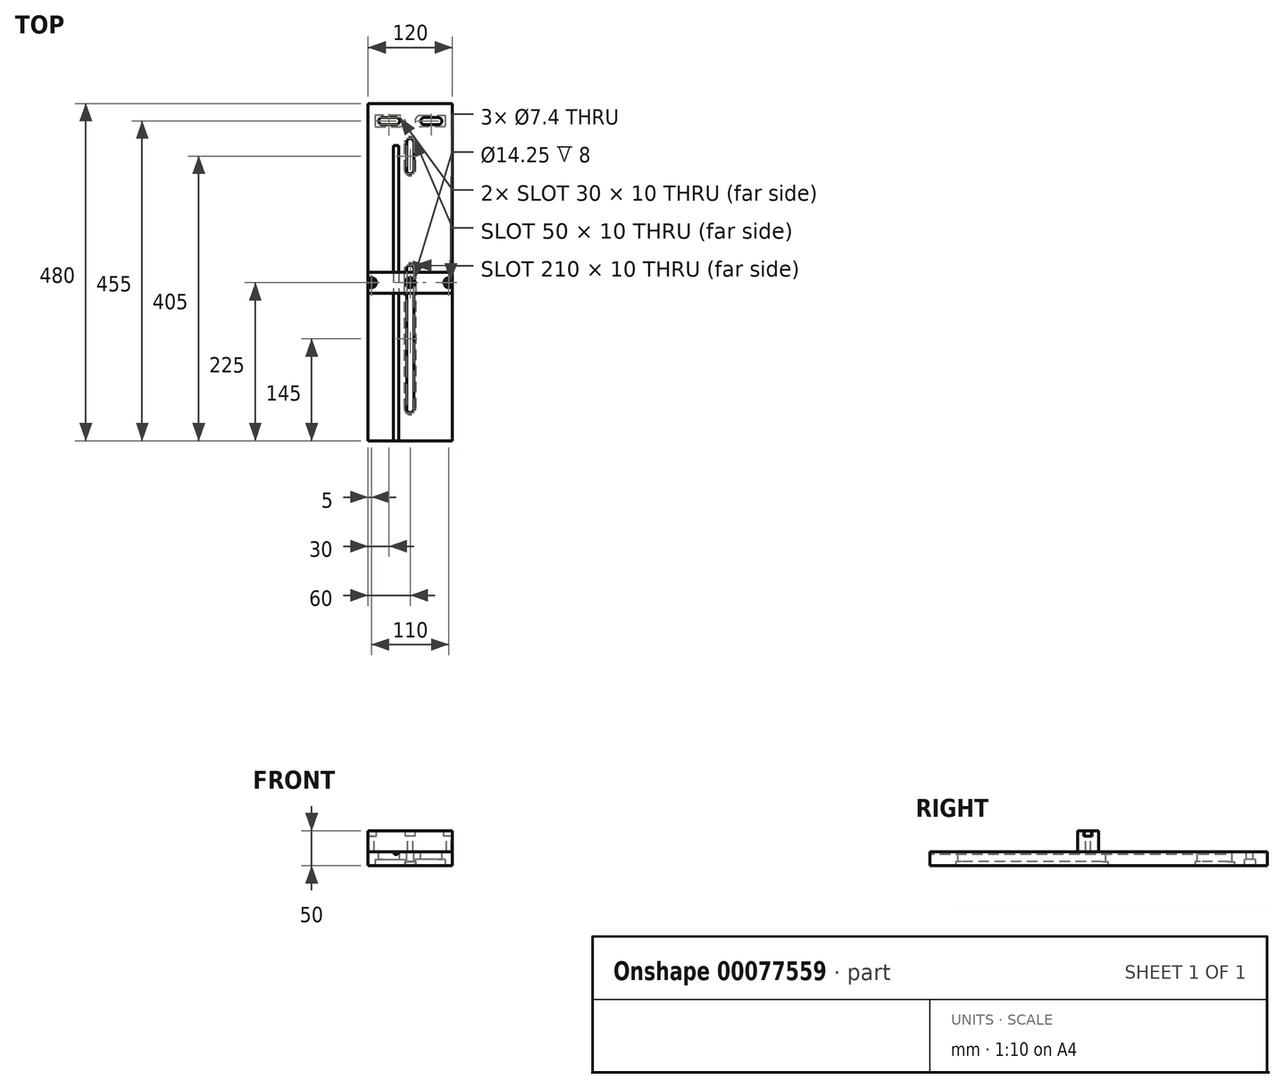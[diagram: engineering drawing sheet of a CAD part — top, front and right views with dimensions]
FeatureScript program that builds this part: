
annotation { "Feature Type Name" : "Feature", "Feature Type Description" : "" }
export const myFeature = defineFeature(function(context is Context, id is Id, definition is map)
    precondition{}
    {
        {
            var Q0;
            Q0=qCreatedBy(makeId("Front.planeOp"),FACE);
            var sketch = newSketch(context, id + "F0", { "sketchPlane" : qUnion([Q0])});
            skLineSegment(sketch, "E0.bottom", {"start": v(-60, 0) * mm, "end": v(60, 0) * mm});
            skLineSegment(sketch, "E0.top", {"start": v(-60, 20) * mm, "end": v(60, 20) * mm});
            skLineSegment(sketch, "E0.left", {"start": v(-60, 0) * mm, "end": v(-60, 20) * mm});
            skLineSegment(sketch, "E0.right", {"start": v(60, 0) * mm, "end": v(60, 20) * mm});
            skSolve(sketch);
        }
        {
            var Q0;
            Q0=makeQuery(id+"F0.imprint","IMPRINT",FACE,{"disambiguationData":[TD([[makeQuery(id+"F0.imprint","IMPRINT",EDGE,{"derivedFrom":sQuery(id+"F0.wireOp",EDGE,"E0.bottom")}),1.0]])]});
            extrude(context, id + "F1", {"entities" : qUnion([Q0]), "oppositeDirection" : true, "depth" : 480 * mm});
        }
        {
            var Q0;
            Q0=makeQuery(id+"F1.opExtrude","SWEPT_FACE",FACE,{"disambiguationData":[OSD([sQuery(id+"F0.wireOp",EDGE,"E0.top")])]});
            var sketch = newSketch(context, id + "F2", { "sketchPlane" : qUnion([Q0])});
            skLineSegment(sketch, "E1", {"start": v(-5, 245) * mm, "end": v(-5, 45) * mm});
            skArc(sketch, "E2", {"start": v(-5, 45) * mm, "mid": v(0, 40) * mm, "end": v(5, 45) * mm});
            skLineSegment(sketch, "E3", {"start": v(5, 45) * mm, "end": v(5, 245) * mm});
            skArc(sketch, "E4", {"start": v(5, 245) * mm, "mid": v(0, 250) * mm, "end": v(-5, 245) * mm});
            skLineSegment(sketch, "E5", {"start": v(0, 425) * mm, "end": v(0, 385) * mm});
            skArc(sketch, "E6.0.startCap", {"start": v(-5, 425) * mm, "mid": v(0, 430) * mm, "end": v(5, 425) * mm});
            skArc(sketch, "E6.0.endCap", {"start": v(5, 385) * mm, "mid": v(0, 380) * mm, "end": v(-5, 385) * mm});
            skLineSegment(sketch, "E6.0.left", {"start": v(5, 425) * mm, "end": v(5, 385) * mm});
            skLineSegment(sketch, "E6.0.right", {"start": v(-5, 425) * mm, "end": v(-5, 385) * mm});
            skSolve(sketch);
        }
        {
            var Q0;
            Q0 = qSketchRegion(id + "F2", true);
            extrude(context, id + "F3", {"entities" : qUnion([Q0]), "operationType" : NewBodyOperationType.REMOVE, "endBound" : BoundingType.THROUGH_ALL, "oppositeDirection" : true, "depth" : 25 * mm});
        }
        {
            var Q0;
            Q0=makeQuery(id+"F1.opExtrude","SWEPT_FACE",FACE,{"disambiguationData":[OSD([sQuery(id+"F0.wireOp",EDGE,"E0.bottom")])]});
            var sketch = newSketch(context, id + "F4", { "sketchPlane" : qUnion([Q0])});
            skArc(sketch, "E7.0", {"start": v(8, -45) * mm, "mid": v(0, -37) * mm, "end": v(-8, -45) * mm});
            skLineSegment(sketch, "E7.1", {"start": v(8, -245) * mm, "end": v(8, -45) * mm});
            skArc(sketch, "E7.2", {"start": v(-8, -245) * mm, "mid": v(0, -253) * mm, "end": v(8, -245) * mm});
            skLineSegment(sketch, "E7.3", {"start": v(-8, -45) * mm, "end": v(-8, -245) * mm});
            skLineSegment(sketch, "E8.0", {"start": v(-8, -385) * mm, "end": v(-8, -425) * mm});
            skArc(sketch, "E8.1", {"start": v(-8, -385) * mm, "mid": v(0, -377) * mm, "end": v(8, -385) * mm});
            skLineSegment(sketch, "E8.2", {"start": v(8, -385) * mm, "end": v(8, -425) * mm});
            skArc(sketch, "E8.3", {"start": v(8, -425) * mm, "mid": v(0, -433) * mm, "end": v(-8, -425) * mm});
            skSolve(sketch);
        }
        {
            var Q0;
            Q0 = qSketchRegion(id + "F4", true);
            extrude(context, id + "F5", {"entities" : qUnion([Q0]), "operationType" : NewBodyOperationType.REMOVE, "oppositeDirection" : true, "depth" : 6.1 * mm});
        }
        {
            var Q0;
            Q0=makeQuery(id+"F1.opExtrude","SWEPT_FACE",FACE,{"disambiguationData":[OSD([sQuery(id+"F0.wireOp",EDGE,"E0.top")])]});
            var sketch = newSketch(context, id + "F6", { "sketchPlane" : qUnion([Q0])});
            skLineSegment(sketch, "E9.bottom", {"start": v(-40, 450) * mm, "end": v(-20, 450) * mm});
            skLineSegment(sketch, "E9.top", {"start": v(-40, 460) * mm, "end": v(-20, 460) * mm});
            skLineSegment(sketch, "E9.left", {"start": v(-45, 455) * mm, "end": v(-45, 455) * mm});
            skLineSegment(sketch, "E9.right", {"start": v(-15, 455) * mm, "end": v(-15, 455) * mm});
            skPoint(sketch, "E10.visualSharp", {"position": v(-45, 460) * mm});
            skArc(sketch, "E10.filletArc", {"start": v(-40, 460) * mm, "mid": v(-43.54, 458.54) * mm, "end": v(-45, 455) * mm});
            skPoint(sketch, "E11.visualSharp", {"position": v(-45, 450) * mm});
            skArc(sketch, "E11.filletArc", {"start": v(-45, 455) * mm, "mid": v(-43.54, 451.46) * mm, "end": v(-40, 450) * mm});
            skPoint(sketch, "E12.visualSharp", {"position": v(-15, 450) * mm});
            skArc(sketch, "E12.filletArc", {"start": v(-20, 450) * mm, "mid": v(-16.46, 451.46) * mm, "end": v(-15, 455) * mm});
            skPoint(sketch, "E13.visualSharp", {"position": v(-15, 460) * mm});
            skArc(sketch, "E13.filletArc", {"start": v(-15, 455) * mm, "mid": v(-16.46, 458.54) * mm, "end": v(-20, 460) * mm});
            skLineSegment(sketch, "E14.MirrorCS", {"start": v(40, 460) * mm, "end": v(20, 460) * mm});
            skArc(sketch, "E15.MirrorCS", {"start": v(15, 455) * mm, "mid": v(16.46, 458.54) * mm, "end": v(20, 460) * mm});
            skArc(sketch, "E16.MirrorCS", {"start": v(20, 450) * mm, "mid": v(16.46, 451.46) * mm, "end": v(15, 455) * mm});
            skLineSegment(sketch, "E17.MirrorCS", {"start": v(40, 450) * mm, "end": v(20, 450) * mm});
            skArc(sketch, "E18.MirrorCS", {"start": v(40, 460) * mm, "mid": v(43.54, 458.54) * mm, "end": v(45, 455) * mm});
            skArc(sketch, "E19.MirrorCS", {"start": v(45, 455) * mm, "mid": v(43.54, 451.46) * mm, "end": v(40, 450) * mm});
            skSolve(sketch);
        }
        {
            var Q0;
            Q0 = qSketchRegion(id + "F6", true);
            extrude(context, id + "F7", {"entities" : qUnion([Q0]), "operationType" : NewBodyOperationType.REMOVE, "endBound" : BoundingType.THROUGH_ALL, "oppositeDirection" : true, "depth" : 25 * mm});
        }
        {
            var Q0;
            Q0=makeQuery(id+"F1.opExtrude","SWEPT_FACE",FACE,{"disambiguationData":[OSD([sQuery(id+"F0.wireOp",EDGE,"E0.bottom")])]});
            var sketch = newSketch(context, id + "F8", { "sketchPlane" : qUnion([Q0])});
            skLineSegment(sketch, "E20", {"start": v(0, -480) * mm, "end": v(0, -420.94) * mm});
            skPoint(sketch, "E20.endSnap0", {"position": v(0, -480) * mm});
            skLineSegment(sketch, "E21", {"start": v(-50, -447) * mm, "end": v(-15, -447) * mm});
            skArc(sketch, "E22", {"start": v(-15, -447) * mm, "mid": v(-7, -455) * mm, "end": v(-15, -463) * mm});
            skLineSegment(sketch, "E23", {"start": v(-15, -463) * mm, "end": v(-50, -463) * mm});
            skLineSegment(sketch, "E24", {"start": v(-50, -463) * mm, "end": v(-50, -447) * mm});
            skArc(sketch, "E25.MirrorCS", {"start": v(15, -447) * mm, "mid": v(7, -455) * mm, "end": v(15, -463) * mm});
            skLineSegment(sketch, "E26.MirrorCS", {"start": v(50, -447) * mm, "end": v(15, -447) * mm});
            skLineSegment(sketch, "E27.MirrorCS", {"start": v(50, -463) * mm, "end": v(50, -447) * mm});
            skLineSegment(sketch, "E28.MirrorCS", {"start": v(15, -463) * mm, "end": v(50, -463) * mm});
            skSolve(sketch);
        }
        {
            var Q0;
            Q0 = qSketchRegion(id + "F8", true);
            extrude(context, id + "F9", {"entities" : qUnion([Q0]), "operationType" : NewBodyOperationType.REMOVE, "oppositeDirection" : true, "depth" : 9 * mm});
        }
        {
            var Q0;
            Q0=makeQuery(id+"F1.opExtrude","CAP_FACE",FACE,{"disambiguationData":[OSD([sQuery(id+"F0.wireOp",EDGE,"E0.bottom"),sQuery(id+"F0.wireOp",EDGE,"E0.top"),sQuery(id+"F0.wireOp",EDGE,"E0.left"),sQuery(id+"F0.wireOp",EDGE,"E0.right")])],"isStart":true});
            var sketch = newSketch(context, id + "F10", { "sketchPlane" : qUnion([Q0])});
            skCircle(sketch, "E29", {"center": v(-20, 20) * mm, "radius": 4 * mm});
            skCircle(sketch, "E30.MirrorC", {"center": v(20, 20) * mm, "radius": 4 * mm});
            skSolve(sketch);
        }
        {
            var Q0;
            {var subQ0=sQuery(id+"F10.wireOp",EDGE,"E29");var subQ1=makeQuery(id+"F1.opExtrude","CAP_EDGE",EDGE,{"disambiguationData":[OSD([sQuery(id+"F0.wireOp",EDGE,"E0.top")])],"isStart":true});var subQ2=makeQuery(id+"F10.imprint","INTERSECT",VERTEX,{"disambiguationData":[OD(0.0)],"derivedFrom":[subQ1,subQ0]});Q0=makeQuery(id+"F10.imprint","IMPRINT",FACE,{"disambiguationData":[TD([[makeQuery(id+"F10.imprint","IMPRINT",EDGE,{"disambiguationData":[TD([[subQ2,-1.0]])],"derivedFrom":subQ0}),1.0]])]});}
            var Q1;
            {var subQ0=sQuery(id+"F10.wireOp",EDGE,"E30.MirrorC");var subQ1=makeQuery(id+"F1.opExtrude","CAP_EDGE",EDGE,{"disambiguationData":[OSD([sQuery(id+"F0.wireOp",EDGE,"E0.top")])],"isStart":true});var subQ2=makeQuery(id+"F10.imprint","INTERSECT",VERTEX,{"disambiguationData":[OD(0.0)],"derivedFrom":[subQ1,subQ0]});Q1=makeQuery(id+"F10.imprint","IMPRINT",FACE,{"disambiguationData":[TD([[makeQuery(id+"F10.imprint","IMPRINT",EDGE,{"disambiguationData":[TD([[subQ2,-1.0]])],"derivedFrom":subQ0}),-1.0]])]});}
            extrude(context, id + "F11", {"entities" : qUnion([Q0, Q1]), "operationType" : NewBodyOperationType.REMOVE, "oppositeDirection" : true, "depth" : 420 * mm});
        }
        {
            var Q0;
            Q0=makeQuery(id+"F1.opExtrude","SWEPT_FACE",FACE,{"disambiguationData":[OSD([sQuery(id+"F0.wireOp",EDGE,"E0.top")])]});
            var sketch = newSketch(context, id + "F12", { "sketchPlane" : qUnion([Q0])});
            skLineSegment(sketch, "E31.bottom", {"start": v(-60, 240) * mm, "end": v(60, 240) * mm});
            skLineSegment(sketch, "E31.top", {"start": v(-60, 210) * mm, "end": v(60, 210) * mm});
            skLineSegment(sketch, "E31.left", {"start": v(-60, 240) * mm, "end": v(-60, 210) * mm});
            skLineSegment(sketch, "E31.right", {"start": v(60, 240) * mm, "end": v(60, 210) * mm});
            skSolve(sketch);
        }
        {
            var Q0;
            Q0 = qSketchRegion(id + "F12", true);
            var Q1;
            Q1 = qSketchRegion(id + "F14", true);
            extrude(context, id + "F13", {"entities" : qUnion([Q0, Q1]), "depth" : 30 * mm});
        }
        {
            var Q0;
            Q0=makeQuery(id+"F13.opExtrude","CAP_FACE",FACE,{"disambiguationData":[OSD([sQuery(id+"F12.wireOp",EDGE,"E31.bottom"),sQuery(id+"F12.wireOp",EDGE,"E31.top"),sQuery(id+"F12.wireOp",EDGE,"E31.left"),sQuery(id+"F12.wireOp",EDGE,"E31.right")])],"isStart":false});
            var Q1;
            Q1=makeQuery(id+"F13.opExtrude","CAP_FACE",FACE,{"disambiguationData":[OSD([sQuery(id+"F12.wireOp",EDGE,"E31.bottom"),sQuery(id+"F12.wireOp",EDGE,"E31.top"),sQuery(id+"F12.wireOp",EDGE,"E31.left"),sQuery(id+"F12.wireOp",EDGE,"E31.right")])],"isStart":false});
            var sketch = newSketch(context, id + "F14", { "sketchPlane" : qUnion([Q0, Q1])});
            skPoint(sketch, "E32", {"position": v(-55, 225) * mm});
            skPoint(sketch, "E32.positionSnap0", {"position": v(-60, 225) * mm});
            skPoint(sketch, "E33", {"position": v(55, 225) * mm});
            skPoint(sketch, "E34", {"position": v(0, 225) * mm});
            skSolve(sketch);
        }
        {
            var Q0;
            Q0=sQuery(id+"F14.wireOp",VERTEX,"E32");
            var Q1;
            Q1=sQuery(id+"F14.wireOp",VERTEX,"E33");
            var Q2;
            Q2=sQuery(id+"F14.wireOp",VERTEX,"E34");
            var Q3;
            Q3=makeQuery(id+"F13.opExtrude","SWEPT_BODY",BODY,{"disambiguationData":[OSD([sQuery(id+"F12.wireOp",EDGE,"E31.bottom"),sQuery(id+"F12.wireOp",EDGE,"E31.top"),sQuery(id+"F12.wireOp",EDGE,"E31.left"),sQuery(id+"F12.wireOp",EDGE,"E31.right")])]});
            hole(context, id + "F15", {"style" : HoleStyle.C_BORE, "endStyle" : HoleEndStyle.BLIND, "standardTappedOrClearance" : lookupTablePath({ "standard" : "ISO", "engagement" : "25%", "pitch" : "1 mm", "size" : "M8", "type" : "Tapped" }), "standardBlindInLast" : lookupTablePath({ "standard" : "ISO", "engagement" : "25%", "pitch" : "1 mm", "size" : "M8", "type" : "Tapped" }), "holeDiameter" : 7.4 * mm, "cBoreDiameter" : 14.25 * mm, "cBoreDepth" : 8 * mm, "holeDepth" : 50 * mm, "startFromSketch" : true, "locations" : qUnion([Q0, Q1, Q2]), "scope" : qUnion([Q3])});
        }
    });
